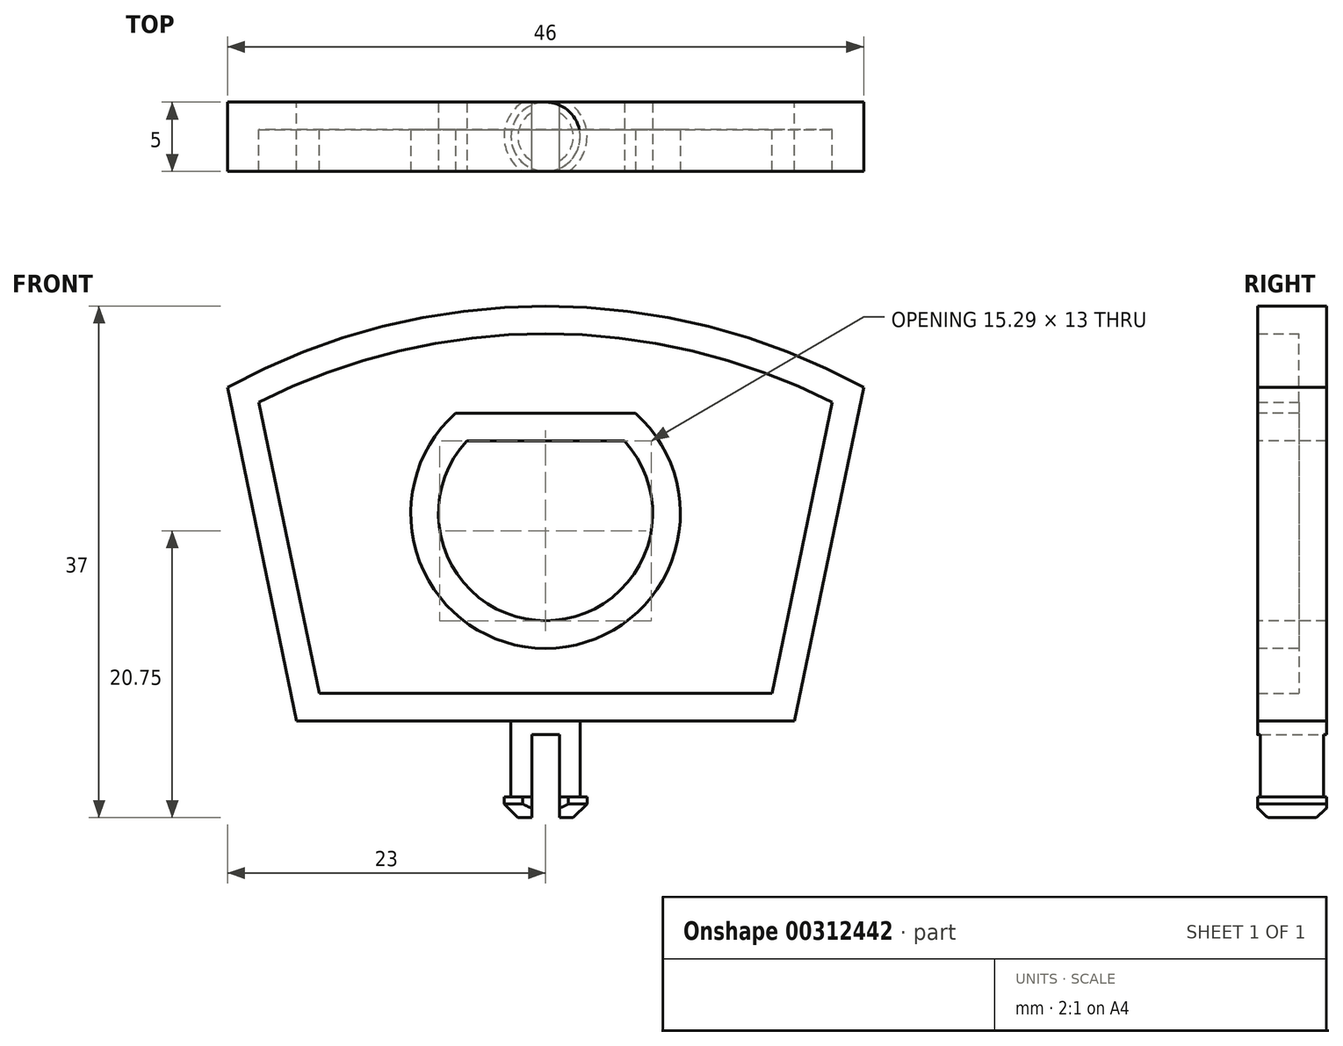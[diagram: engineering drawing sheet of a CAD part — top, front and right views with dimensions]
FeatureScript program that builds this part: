
annotation { "Feature Type Name" : "Feature", "Feature Type Description" : "" }
export const myFeature = defineFeature(function(context is Context, id is Id, definition is map)
    precondition{}
    {
        {
            var Q0;
            Q0=qCreatedBy(makeId("Front.planeOp"),FACE);
            var sketch = newSketch(context, id + "F0", { "sketchPlane" : qUnion([Q0])});
            skLineSegment(sketch, "E0", {"start": v(-23, 24.13) * mm, "end": v(-18, 0) * mm});
            skLineSegment(sketch, "E1", {"start": v(-18, 0) * mm, "end": v(18, 0) * mm});
            skLineSegment(sketch, "E2", {"start": v(18, 0) * mm, "end": v(23, 24.13) * mm});
            skArc(sketch, "E3", {"start": v(23, 24.13) * mm, "mid": v(0, 30) * mm, "end": v(-23, 24.13) * mm});
            skSolve(sketch);
        }
        {
            var Q0;
            Q0 = qSketchRegion(id + "F0", true);
            extrude(context, id + "F1", {"entities" : qUnion([Q0]), "endBound" : BoundingType.SYMMETRIC, "depth" : 5 * mm});
        }
        {
            var Q0;
            Q0=makeQuery(id+"F1.opExtrude","CAP_FACE",FACE,{"disambiguationData":[OSD([sQuery(id+"F0.wireOp",EDGE,"E0"),sQuery(id+"F0.wireOp",EDGE,"E1"),sQuery(id+"F0.wireOp",EDGE,"E2"),sQuery(id+"F0.wireOp",EDGE,"E3")])],"isStart":false});
            var sketch = newSketch(context, id + "F2", { "sketchPlane" : qUnion([Q0])});
            skLineSegment(sketch, "E4", {"start": v(-5.7, 20.25) * mm, "end": v(5.7, 20.25) * mm});
            skArc(sketch, "E5", {"start": v(-5.7, 20.25) * mm, "mid": v(0, 7.25) * mm, "end": v(5.7, 20.25) * mm});
            skSolve(sketch);
        }
        {
            var Q0;
            Q0=makeQuery(id+"F2.imprint","IMPRINT",FACE,{"disambiguationData":[TD([[makeQuery(id+"F2.imprint","IMPRINT",EDGE,{"derivedFrom":sQuery(id+"F2.wireOp",EDGE,"E4")}),-1.0]])]});
            extrude(context, id + "F3", {"entities" : qUnion([Q0]), "operationType" : NewBodyOperationType.REMOVE, "oppositeDirection" : true, "depth" : 25 * mm});
        }
        {
            var Q0;
            Q0=makeQuery(id+"F1.opExtrude","CAP_FACE",FACE,{"disambiguationData":[OSD([sQuery(id+"F0.wireOp",EDGE,"E0"),sQuery(id+"F0.wireOp",EDGE,"E1"),sQuery(id+"F0.wireOp",EDGE,"E2"),sQuery(id+"F0.wireOp",EDGE,"E3")])],"isStart":false});
            shell(context, id + "F4", {"entities" : qUnion([Q0]), "thickness" : 2 * mm});
        }
        {
            var Q0;
            Q0=qCreatedBy(makeId("Front.planeOp"),FACE);
            var sketch = newSketch(context, id + "F5", { "sketchPlane" : qUnion([Q0])});
            skLineSegment(sketch, "E6", {"start": v(-2.5, 0) * mm, "end": v(-2.5, -5.5) * mm});
            skLineSegment(sketch, "E7", {"start": v(-2.5, -5.5) * mm, "end": v(-3, -5.5) * mm});
            skLineSegment(sketch, "E8", {"start": v(-3, -5.5) * mm, "end": v(-3, -7) * mm});
            skLineSegment(sketch, "E9", {"start": v(-3, -7) * mm, "end": v(0, -7) * mm});
            skLineSegment(sketch, "E10", {"start": v(0, 0) * mm, "end": v(0, -7) * mm});
            skLineSegment(sketch, "E11", {"start": v(-2.5, 0) * mm, "end": v(0, 0) * mm});
            skSolve(sketch);
        }
        {
            var Q0;
            Q0 = qSketchRegion(id + "F5", true);
            var Q1;
            Q1=sQuery(id+"F5.wireOp",EDGE,"E10");
            revolve(context, id + "F6", {"entities" : qUnion([Q0]), "axis" : qUnion([Q1]), "revolveType" : RevolveType.FULL});
        }
        {
            var Q0;
            Q0=makeQuery(id+"F6.opRevolve","SWEPT_EDGE",EDGE,{"disambiguationData":[OSD([sQuery(id+"F5.wireOp",EDGE,"E8"),sQuery(id+"F5.wireOp",EDGE,"E9")])]});
            chamfer(context, id + "F7", {"entities" : qUnion([Q0]), "width" : 1 * mm, "tangentPropagation" : true});
        }
        {
            var Q0;
            Q0=makeQuery(id+"F6.opRevolve","SWEPT_FACE",FACE,{"disambiguationData":[OSD([sQuery(id+"F5.wireOp",EDGE,"E9")])]});
            var sketch = newSketch(context, id + "F8", { "sketchPlane" : qUnion([Q0])});
            skLineSegment(sketch, "E12.bottom", {"start": v(0, 3.4) * mm, "end": v(-1, 3.4) * mm});
            skLineSegment(sketch, "E12.top", {"start": v(0, -4.22) * mm, "end": v(-1, -4.22) * mm});
            skLineSegment(sketch, "E12.left", {"start": v(0, 3.4) * mm, "end": v(0, -4.22) * mm});
            skLineSegment(sketch, "E12.right", {"start": v(-1, 3.4) * mm, "end": v(-1, -4.22) * mm});
            skLineSegment(sketch, "E13.bottom", {"start": v(0, 3.4) * mm, "end": v(1, 3.4) * mm});
            skLineSegment(sketch, "E13.top", {"start": v(0, -4.22) * mm, "end": v(1, -4.22) * mm});
            skLineSegment(sketch, "E13.right", {"start": v(1, 3.4) * mm, "end": v(1, -4.22) * mm});
            skSolve(sketch);
        }
        {
            var Q0;
            Q0 = qSketchRegion(id + "F8", true);
            extrude(context, id + "F9", {"entities" : qUnion([Q0]), "operationType" : NewBodyOperationType.REMOVE, "oppositeDirection" : true, "depth" : 6 * mm});
        }
        {
            var Q0;
            {var subQ0=sQuery(id+"F5.wireOp",EDGE,"E9");Q0=makeQuery(id+"F9.boolean.opBoolean","SPLIT",FACE,{"disambiguationData":[TD([makeQuery(id+"F9.opExtrude","SWEPT_FACE",FACE,{"disambiguationData":[OSD([sQuery(id+"F8.wireOp",EDGE,"E13.right")])]})])],"derivedFrom":makeQuery(id+"F6.opRevolve","SWEPT_FACE",FACE,{"disambiguationData":[OSD([subQ0])]})});}
            var sketch = newSketch(context, id + "F10", { "sketchPlane" : qUnion([Q0])});
            skLineSegment(sketch, "E14.bottom", {"start": v(-33.95, 2.5) * mm, "end": v(27.22, 2.5) * mm});
            skLineSegment(sketch, "E14.top", {"start": v(-33.95, -2.5) * mm, "end": v(27.22, -2.5) * mm});
            skLineSegment(sketch, "E14.left", {"start": v(-33.95, 2.5) * mm, "end": v(-33.95, -2.5) * mm});
            skLineSegment(sketch, "E14.right", {"start": v(27.22, 2.5) * mm, "end": v(27.22, -2.5) * mm});
            skSolve(sketch);
        }
        {
            var Q0;
            Q0 = qSketchRegion(id + "F10", true);
            extrude(context, id + "F11", {"entities" : qUnion([Q0]), "operationType" : NewBodyOperationType.INTERSECT, "endBound" : BoundingType.THROUGH_ALL, "oppositeDirection" : true, "depth" : 25 * mm});
        }
    });
